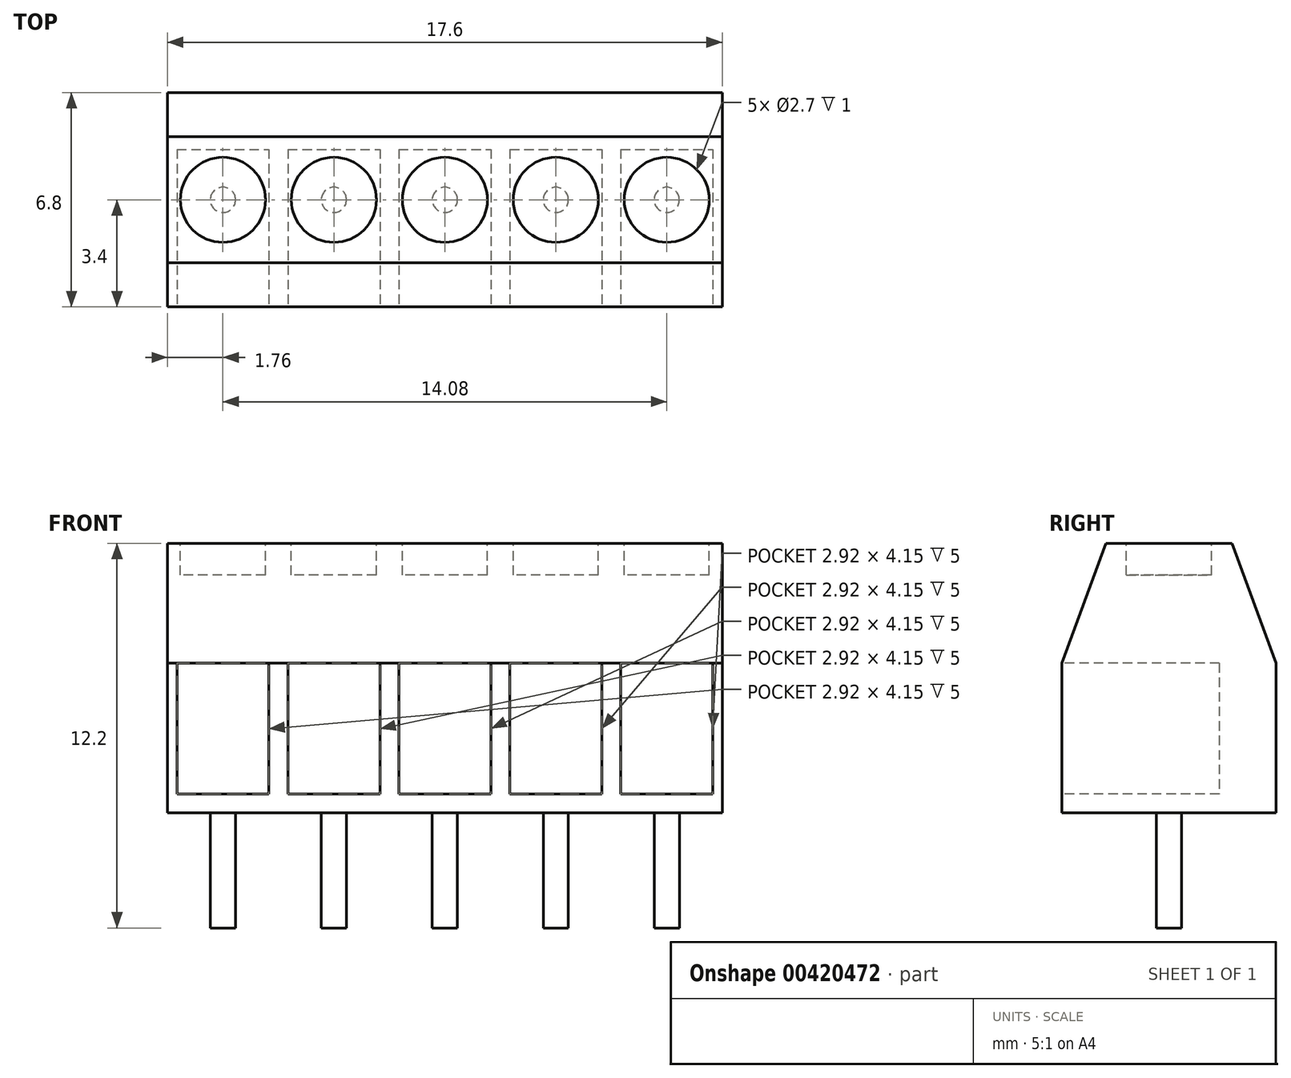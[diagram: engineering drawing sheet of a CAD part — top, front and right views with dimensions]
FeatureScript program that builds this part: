
annotation { "Feature Type Name" : "Feature", "Feature Type Description" : "" }
export const myFeature = defineFeature(function(context is Context, id is Id, definition is map)
    precondition{}
    {
        {
            var Q0;
            Q0=qCreatedBy(makeId("Front.planeOp"),FACE);
            var sketch = newSketch(context, id + "F0", { "sketchPlane" : qUnion([Q0])});
            skLineSegment(sketch, "E0.bottom", {"start": v(0, 0) * mm, "end": v(17.6, 0) * mm});
            skLineSegment(sketch, "E0.top", {"start": v(0, 8.55) * mm, "end": v(17.6, 8.55) * mm});
            skLineSegment(sketch, "E0.left", {"start": v(0, 0) * mm, "end": v(0, 8.55) * mm});
            skLineSegment(sketch, "E0.right", {"start": v(17.6, 0) * mm, "end": v(17.6, 8.55) * mm});
            skSolve(sketch);
        }
        {
            var Q0;
            Q0 = qSketchRegion(id + "F0", true);
            extrude(context, id + "F1", {"entities" : qUnion([Q0]), "depth" : 6.8 * mm});
        }
        {
            var Q0;
            Q0=makeQuery(id+"F1.opExtrude","SWEPT_FACE",FACE,{"disambiguationData":[OSD([sQuery(id+"F0.wireOp",EDGE,"E0.right")])]});
            var sketch = newSketch(context, id + "F2", { "sketchPlane" : qUnion([Q0])});
            skLineSegment(sketch, "E1", {"start": v(-5.4, 8.55) * mm, "end": v(-6.8, 4.75) * mm});
            skLineSegment(sketch, "E2", {"start": v(-6.8, 4.75) * mm, "end": v(-6.8, 8.55) * mm});
            skLineSegment(sketch, "E3", {"start": v(-6.8, 8.55) * mm, "end": v(-5.4, 8.55) * mm});
            skLineSegment(sketch, "E4", {"start": v(-3.4, 8.55) * mm, "end": v(-3.4, 0) * mm, "construction": true});
            skLineSegment(sketch, "E5.MirrorCS", {"start": v(0, 4.75) * mm, "end": v(0, 8.55) * mm});
            skLineSegment(sketch, "E6.MirrorCS", {"start": v(-1.4, 8.55) * mm, "end": v(0, 4.75) * mm});
            skLineSegment(sketch, "E7.MirrorCS", {"start": v(0, 8.55) * mm, "end": v(-1.4, 8.55) * mm});
            skSolve(sketch);
        }
        {
            var Q0;
            Q0 = qSketchRegion(id + "F2", true);
            extrude(context, id + "F3", {"entities" : qUnion([Q0]), "operationType" : NewBodyOperationType.REMOVE, "endBound" : BoundingType.UP_TO_NEXT, "oppositeDirection" : true, "depth" : 25 * mm});
        }
        {
            var Q0;
            Q0=makeQuery(id+"F1.opExtrude","CAP_FACE",FACE,{"disambiguationData":[OSD([sQuery(id+"F0.wireOp",EDGE,"E0.bottom"),sQuery(id+"F0.wireOp",EDGE,"E0.top"),sQuery(id+"F0.wireOp",EDGE,"E0.left"),sQuery(id+"F0.wireOp",EDGE,"E0.right")])],"isStart":false});
            var sketch = newSketch(context, id + "F4", { "sketchPlane" : qUnion([Q0])});
            skLineSegment(sketch, "E8.bottom", {"start": v(0.3, 4.75) * mm, "end": v(3.22, 4.75) * mm});
            skLineSegment(sketch, "E8.top", {"start": v(0.3, 0.6) * mm, "end": v(3.22, 0.6) * mm});
            skLineSegment(sketch, "E8.left", {"start": v(0.3, 4.75) * mm, "end": v(0.3, 0.6) * mm});
            skLineSegment(sketch, "E8.right", {"start": v(3.22, 4.75) * mm, "end": v(3.22, 0.6) * mm});
            skLineSegment(sketch, "E9", {"start": v(3.52, 4.75) * mm, "end": v(3.52, 0) * mm, "construction": true});
            skLineSegment(sketch, "E10", {"start": v(7.04, 4.75) * mm, "end": v(7.04, 0) * mm, "construction": true});
            skLineSegment(sketch, "E11", {"start": v(10.56, 4.75) * mm, "end": v(10.56, 0) * mm, "construction": true});
            skLineSegment(sketch, "E12", {"start": v(14.08, 4.75) * mm, "end": v(14.08, 0) * mm, "construction": true});
            skLineSegment(sketch, "E13.bottom", {"start": v(3.82, 4.75) * mm, "end": v(6.74, 4.75) * mm});
            skLineSegment(sketch, "E13.top", {"start": v(3.82, 0.6) * mm, "end": v(6.74, 0.6) * mm});
            skLineSegment(sketch, "E13.left", {"start": v(3.82, 4.75) * mm, "end": v(3.82, 0.6) * mm});
            skLineSegment(sketch, "E13.right", {"start": v(6.74, 4.75) * mm, "end": v(6.74, 0.6) * mm});
            skLineSegment(sketch, "E14.bottom", {"start": v(7.34, 4.75) * mm, "end": v(10.26, 4.75) * mm});
            skLineSegment(sketch, "E14.top", {"start": v(7.34, 0.6) * mm, "end": v(10.26, 0.6) * mm});
            skLineSegment(sketch, "E14.left", {"start": v(7.34, 4.75) * mm, "end": v(7.34, 0.6) * mm});
            skLineSegment(sketch, "E14.right", {"start": v(10.26, 4.75) * mm, "end": v(10.26, 0.6) * mm});
            skLineSegment(sketch, "E15.bottom", {"start": v(10.86, 4.75) * mm, "end": v(13.78, 4.75) * mm});
            skLineSegment(sketch, "E15.top", {"start": v(10.86, 0.6) * mm, "end": v(13.78, 0.6) * mm});
            skLineSegment(sketch, "E15.left", {"start": v(10.86, 4.75) * mm, "end": v(10.86, 0.6) * mm});
            skLineSegment(sketch, "E15.right", {"start": v(13.78, 4.75) * mm, "end": v(13.78, 0.6) * mm});
            skLineSegment(sketch, "E16.bottom", {"start": v(14.38, 4.75) * mm, "end": v(17.3, 4.75) * mm});
            skLineSegment(sketch, "E16.top", {"start": v(14.38, 0.6) * mm, "end": v(17.3, 0.6) * mm});
            skLineSegment(sketch, "E16.left", {"start": v(14.38, 4.75) * mm, "end": v(14.38, 0.6) * mm});
            skLineSegment(sketch, "E16.right", {"start": v(17.3, 4.75) * mm, "end": v(17.3, 0.6) * mm});
            skSolve(sketch);
        }
        {
            var Q0;
            Q0 = qSketchRegion(id + "F4", true);
            extrude(context, id + "F5", {"entities" : qUnion([Q0]), "operationType" : NewBodyOperationType.REMOVE, "oppositeDirection" : true, "depth" : 5 * mm});
        }
        {
            var Q0;
            Q0=makeQuery(id+"F1.opExtrude","SWEPT_FACE",FACE,{"disambiguationData":[OSD([sQuery(id+"F0.wireOp",EDGE,"E0.top")])]});
            var sketch = newSketch(context, id + "F6", { "sketchPlane" : qUnion([Q0])});
            skLineSegment(sketch, "E17", {"start": v(3.52, -1.4) * mm, "end": v(3.52, -5.4) * mm, "construction": true});
            skLineSegment(sketch, "E18", {"start": v(7.04, -1.4) * mm, "end": v(7.04, -5.4) * mm, "construction": true});
            skLineSegment(sketch, "E19", {"start": v(10.56, -1.4) * mm, "end": v(10.56, -5.4) * mm, "construction": true});
            skLineSegment(sketch, "E20", {"start": v(14.08, -1.4) * mm, "end": v(14.08, -5.4) * mm, "construction": true});
            skCircle(sketch, "E21", {"center": v(1.76, -3.4) * mm, "radius": 1.35 * mm});
            skCircle(sketch, "E22", {"center": v(5.28, -3.4) * mm, "radius": 1.35 * mm});
            skCircle(sketch, "E23", {"center": v(8.8, -3.4) * mm, "radius": 1.35 * mm});
            skCircle(sketch, "E24", {"center": v(12.32, -3.4) * mm, "radius": 1.35 * mm});
            skCircle(sketch, "E25", {"center": v(15.84, -3.4) * mm, "radius": 1.35 * mm});
            skLineSegment(sketch, "E26", {"start": v(0, -3.4) * mm, "end": v(17.6, -3.4) * mm, "construction": true});
            skSolve(sketch);
        }
        {
            var Q0;
            Q0 = qSketchRegion(id + "F6", true);
            extrude(context, id + "F7", {"entities" : qUnion([Q0]), "operationType" : NewBodyOperationType.REMOVE, "oppositeDirection" : true, "depth" : 1 * mm});
        }
        {
            var Q0;
            Q0=makeQuery(id+"F1.opExtrude","SWEPT_FACE",FACE,{"disambiguationData":[OSD([sQuery(id+"F0.wireOp",EDGE,"E0.bottom")])]});
            var sketch = newSketch(context, id + "F8", { "sketchPlane" : qUnion([Q0])});
            skLineSegment(sketch, "E27", {"start": v(1.76, 6.8) * mm, "end": v(1.76, 0) * mm, "construction": true});
            skLineSegment(sketch, "E28", {"start": v(5.28, 6.8) * mm, "end": v(5.28, 0) * mm, "construction": true});
            skLineSegment(sketch, "E29", {"start": v(8.8, 6.8) * mm, "end": v(8.8, 0) * mm, "construction": true});
            skLineSegment(sketch, "E30", {"start": v(12.32, 6.8) * mm, "end": v(12.32, 0) * mm, "construction": true});
            skLineSegment(sketch, "E31", {"start": v(15.84, 6.8) * mm, "end": v(15.84, 0) * mm, "construction": true});
            skCircle(sketch, "E32", {"center": v(1.76, 3.4) * mm, "radius": 0.4 * mm});
            skCircle(sketch, "E33", {"center": v(5.28, 3.4) * mm, "radius": 0.4 * mm});
            skCircle(sketch, "E34", {"center": v(8.8, 3.4) * mm, "radius": 0.4 * mm});
            skCircle(sketch, "E35", {"center": v(12.32, 3.4) * mm, "radius": 0.4 * mm});
            skCircle(sketch, "E36", {"center": v(15.84, 3.4) * mm, "radius": 0.4 * mm});
            skSolve(sketch);
        }
        {
            var Q0;
            Q0 = qSketchRegion(id + "F8", true);
            extrude(context, id + "F9", {"entities" : qUnion([Q0]), "operationType" : NewBodyOperationType.ADD, "depth" : 3.65 * mm});
        }
    });
